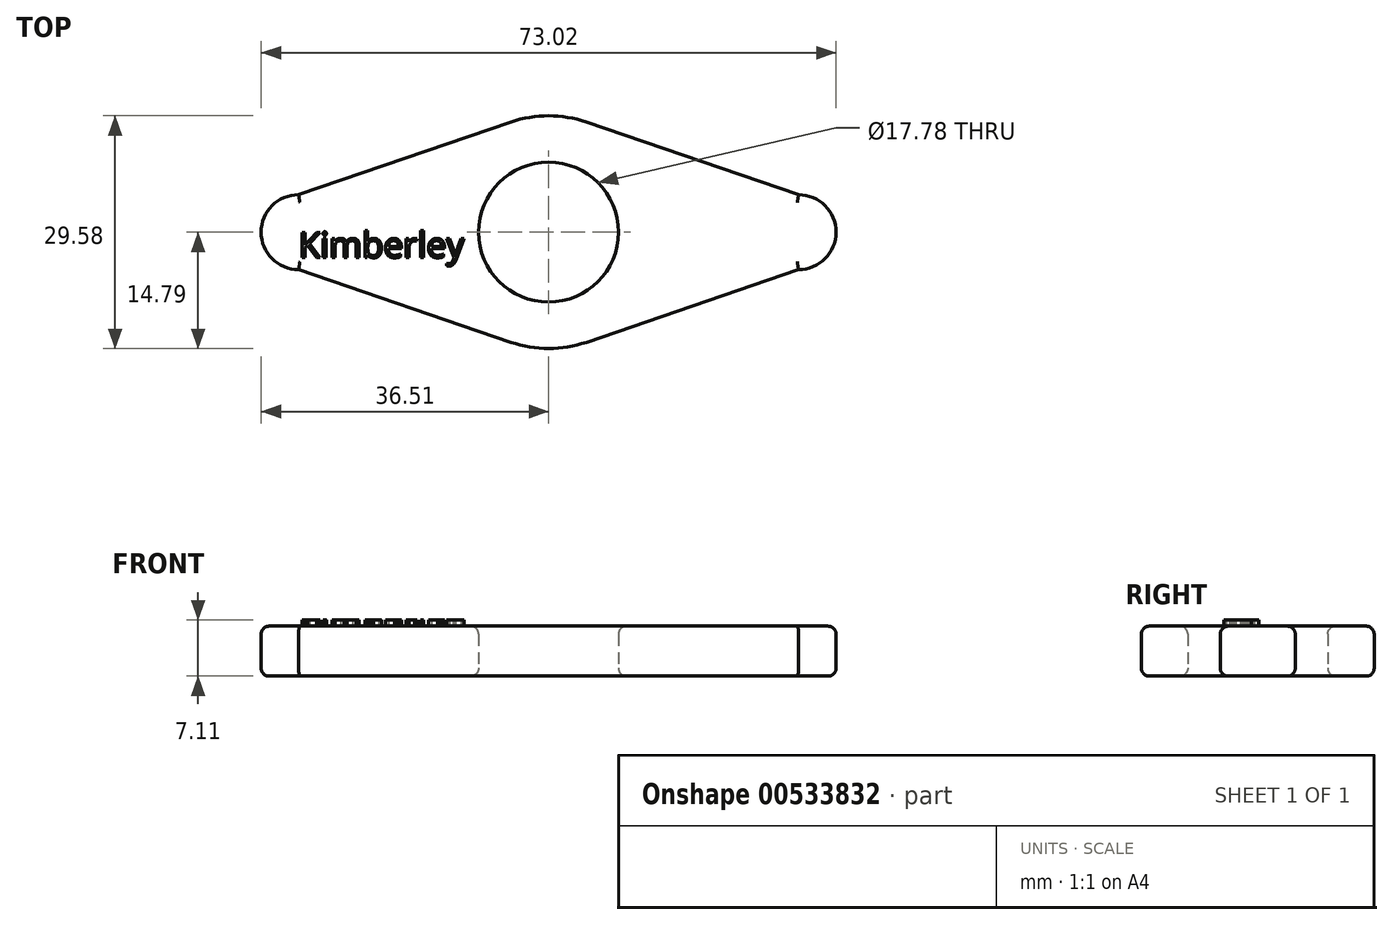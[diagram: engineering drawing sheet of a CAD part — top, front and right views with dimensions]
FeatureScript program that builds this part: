
annotation { "Feature Type Name" : "Feature", "Feature Type Description" : "" }
export const myFeature = defineFeature(function(context is Context, id is Id, definition is map)
    precondition{}
    {
        {
            var Q0;
            Q0=qCreatedBy(makeId("Top.planeOp"),FACE);
            var sketch = newSketch(context, id + "F0", { "sketchPlane" : qUnion([Q0])});
            skLineSegment(sketch, "E0.right", {"start": v(-63.5, -23.81) * mm, "end": v(-63.5, -38.1) * mm});
            skCircle(sketch, "E1", {"center": v(-31.75, -19.05) * mm, "radius": 8.9 * mm});
            skPoint(sketch, "E1.centerSnap0", {"position": v(-63.5, -19.05) * mm});
            skPoint(sketch, "E1.centerSnap1", {"position": v(-31.75, 0) * mm});
            skArc(sketch, "E2", {"start": v(0, -23.81) * mm, "mid": v(4.76, -19.05) * mm, "end": v(0, -14.29) * mm});
            skArc(sketch, "E3", {"start": v(-63.5, -14.29) * mm, "mid": v(-68.26, -19.05) * mm, "end": v(-63.5, -23.81) * mm});
            skArc(sketch, "E4", {"start": v(-36.54, -33.04) * mm, "mid": v(-31.75, -33.84) * mm, "end": v(-26.96, -33.04) * mm});
            skLineSegment(sketch, "E5", {"start": v(0, -14.29) * mm, "end": v(-26.96, -5.06) * mm});
            skLineSegment(sketch, "E6.MirrorCS", {"start": v(-63.5, -14.29) * mm, "end": v(-36.54, -5.06) * mm});
            skLineSegment(sketch, "E7.MirrorCS", {"start": v(-63.5, -23.81) * mm, "end": v(-36.54, -33.04) * mm});
            skLineSegment(sketch, "E8.MirrorCS", {"start": v(0, -23.81) * mm, "end": v(-26.96, -33.04) * mm});
            skPoint(sketch, "E9.orphan", {"position": v(-63.5, 0) * mm});
            skLineSegment(sketch, "E10.trimOffspring", {"start": v(-31.75, -27.94) * mm, "end": v(-31.75, -33.84) * mm});
            skPoint(sketch, "E11.orphan", {"position": v(-31.75, -38.1) * mm});
            skArc(sketch, "E12.trimOffspring", {"start": v(-26.96, -5.06) * mm, "mid": v(-31.75, -4.26) * mm, "end": v(-36.54, -5.06) * mm});
            skPoint(sketch, "E0.left.start.orphan", {"position": v(0, 0) * mm});
            skPoint(sketch, "E13.orphan", {"position": v(0, -38.1) * mm});
            skSolve(sketch);
        }
        {
            var Q0;
            Q0=makeQuery(id+"F0.imprint","IMPRINT",FACE,{"disambiguationData":[TD([[makeQuery(id+"F0.imprint","IMPRINT",EDGE,{"derivedFrom":sQuery(id+"F0.wireOp",EDGE,"E1")}),-1.0]])]});
            extrude(context, id + "F1", {"entities" : qUnion([Q0]), "depth" : 6.35 * mm, "offsetDistance" : 25.4 * mm});
        }
        {
            var Q0;
            Q0=makeQuery(id+"F1.opExtrude","CAP_FACE",FACE,{"disambiguationData":[OSD([sQuery(id+"F0.wireOp",EDGE,"E1"),sQuery(id+"F0.wireOp",EDGE,"E2"),sQuery(id+"F0.wireOp",EDGE,"E3"),sQuery(id+"F0.wireOp",EDGE,"E4"),sQuery(id+"F0.wireOp",EDGE,"E5"),sQuery(id+"F0.wireOp",EDGE,"E6.MirrorCS"),sQuery(id+"F0.wireOp",EDGE,"E7.MirrorCS"),sQuery(id+"F0.wireOp",EDGE,"E8.MirrorCS"),sQuery(id+"F0.wireOp",EDGE,"E12.trimOffspring")])],"isStart":false});
            var Q1;
            Q1=makeQuery(id+"F1.opExtrude","CAP_FACE",FACE,{"disambiguationData":[OSD([sQuery(id+"F0.wireOp",EDGE,"E1"),sQuery(id+"F0.wireOp",EDGE,"E2"),sQuery(id+"F0.wireOp",EDGE,"E3"),sQuery(id+"F0.wireOp",EDGE,"E4"),sQuery(id+"F0.wireOp",EDGE,"E5"),sQuery(id+"F0.wireOp",EDGE,"E6.MirrorCS"),sQuery(id+"F0.wireOp",EDGE,"E7.MirrorCS"),sQuery(id+"F0.wireOp",EDGE,"E8.MirrorCS"),sQuery(id+"F0.wireOp",EDGE,"E12.trimOffspring")])],"isStart":true});
            fillet(context, id + "F2", {"entities" : qUnion([Q0, Q1]), "radius" : 1.02 * mm, "tangentPropagation" : true, "allowEdgeOverflow" : false});
        }
        {
            var Q0;
            Q0=makeQuery(id+"F1.opExtrude","CAP_FACE",FACE,{"disambiguationData":[OSD([sQuery(id+"F0.wireOp",EDGE,"E1"),sQuery(id+"F0.wireOp",EDGE,"E2"),sQuery(id+"F0.wireOp",EDGE,"E3"),sQuery(id+"F0.wireOp",EDGE,"E4"),sQuery(id+"F0.wireOp",EDGE,"E5"),sQuery(id+"F0.wireOp",EDGE,"E6.MirrorCS"),sQuery(id+"F0.wireOp",EDGE,"E7.MirrorCS"),sQuery(id+"F0.wireOp",EDGE,"E8.MirrorCS"),sQuery(id+"F0.wireOp",EDGE,"E12.trimOffspring")])],"isStart":false});
            var sketch = newSketch(context, id + "F3", { "sketchPlane" : qUnion([Q0])});
            skText(sketch, "E14", { "text": "Kimberley", "fontName": "OpenSans-Regular.ttf"});
            const initialGuessF3  = {"E14": [-0.0635, -0.02227, 1, 0, 0.00322]};
            skSetInitialGuess(sketch, initialGuessF3);
            skSolve(sketch);
        }
        {
            var Q0;
            Q0 = qSketchRegion(id + "F3", true);
            extrude(context, id + "F4", {"entities" : qUnion([Q0]), "operationType" : NewBodyOperationType.ADD, "depth" : 0.76 * mm, "offsetDistance" : 25.4 * mm});
        }
    });
